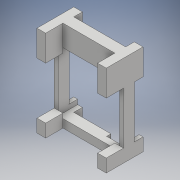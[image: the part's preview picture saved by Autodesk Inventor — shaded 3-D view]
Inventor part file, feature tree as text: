
AUTODESK INVENTOR PART (.ipt)
format: ipt  version: 2017 (Build 210142000, 142)  size: 410,624 bytes
history: native  units: mm
features: sketch x32, extrude x29
ambient origin geometry x8: Origin, YZ Plane, XZ Plane, XY Plane, X Axis, Y Axis, Z Axis, Center Point
bodies: Solid1 (feature_tree)
feature tree (61):
  extrude  "Extrusion1"  Depth=160.0mm
  extrude  "Extrusion2"  Depth=10.0mm
  extrude  "Extrusion3"  Depth=140.0mm
  extrude  "Extrusion4"  Depth=140.0mm TaperAngle=0.0deg
  extrude  "Extrusion5"  Depth=10.0mm
  extrude  "Extrusion6"  Depth=120.0mm
  extrude  "Extrusion7"  Depth=10.0mm
  extrude  "Extrusion8"  Depth=120.0mm
  extrude  "Extrusion9"  Depth=10.0mm
  extrude  "Extrusion10"  Depth=10.0mm
  extrude  "Extrusion11"  Depth=10.0mm TaperAngle=0.0deg
  extrude  "Extrusion12"  Depth=20.0mm
  sketch  "Sketch13"  dims[d29=10.0mm d30=0.0mm d31=10.0mm]
  extrude  "Extrusion13"  Depth=10.0mm
  extrude  "Extrusion14"  Depth=20.0mm
  extrude  "Extrusion15"  Depth=10.0mm
  extrude  "Extrusion16"  Depth=120.0mm
  sketch  "Sketch18"  dims[d42=1.0mm d43=0.0mm d44=1.0mm d45=0.0mm]
  extrude  "Extrusion17"  Depth=10.0mm TaperAngle=0.0deg
  sketch  "Sketch20"  dims[d50=10.0mm d51=0.0mm d52=10.0mm d53=0.0mm]
  extrude  "Extrusion18"  Depth=1.0mm TaperAngle=0.0deg
  extrude  "Extrusion19"  Depth=1.0mm TaperAngle=0.0deg
  extrude  "Extrusion20"  Depth=10.0mm TaperAngle=0.0deg
  extrude  "Extrusion21"  Depth=142.0mm
  extrude  "Extrusion22"  Depth=19.0mm TaperAngle=0.0deg
  extrude  "Extrusion23"  Depth=11.0mm TaperAngle=0.0deg
  extrude  "Extrusion24"  Depth=10.0mm
  extrude  "Extrusion25"  Depth=11.0mm TaperAngle=0.0deg
  extrude  "Extrusion26"  Depth=10.0mm
  extrude  "Extrusion27"  Depth=11.0mm TaperAngle=0.0deg
  extrude  "Extrusion28"  Depth=11.0mm TaperAngle=0.0deg
  extrude  "Extrusion29"  Depth=11.0mm
  sketch  "Sketch1"  dims[d0=160.0mm d1=190.0mm]
  sketch  "Sketch2"  dims[d2=55.0mm d3=0.0mm d4=10.0mm]
  sketch  "Sketch3"  dims[d5=10.0mm d6=140.0mm]
  sketch  "Sketch4"  dims[d7=140.0mm d8=35.0mm d9=0.0mm]
  sketch  "Sketch5"  dims[d10=10.0mm d11=10.0mm]
  sketch  "Sketch6"  dims[d12=120.0mm d13=120.0mm]
  sketch  "Sketch7"  dims[d14=20.0mm d15=0.0mm d16=10.0mm]
  sketch  "Sketch8"  dims[d17=10.0mm d18=120.0mm]
  sketch  "Sketch9"  dims[d19=120.0mm d20=10.0mm]
  sketch  "Sketch10"  dims[d21=120.0mm d22=10.0mm]
  sketch  "Sketch11"  dims[d23=20.0mm d24=0.0mm d25=10.0mm d26=0.0mm]
  sketch  "Sketch12"  dims[d27=120.0mm d28=20.0mm]
  sketch  "Sketch14"  dims[d32=10.0mm d33=20.0mm]
  sketch  "Sketch15"  dims[d34=10.0mm d35=10.0mm]
  sketch  "Sketch16"  dims[d36=45.0mm d37=0.0mm d38=120.0mm]
  sketch  "Sketch17"  dims[d39=20.0mm d40=10.0mm d41=0.0mm]
  sketch  "Sketch19"  dims[d46=1.0mm d47=0.0mm d48=1.0mm d49=0.0mm]
  sketch  "Sketch21"  dims[d54=45.0mm d55=0.0mm d56=142.0mm]
  sketch  "Sketch22"  dims[d57=10.0mm d58=19.0mm d59=0.0mm]
  sketch  "Sketch23"  dims[d60=11.0mm d61=0.0mm d62=11.0mm d63=0.0mm]
  sketch  "Sketch24"  dims[d64=142.0mm d65=10.0mm]
  sketch  "Sketch25"  dims[d66=9.0mm d67=0.0mm d68=11.0mm d69=0.0mm]
  sketch  "Sketch26"  dims[d70=142.0mm d71=10.0mm]
  sketch  "Sketch27"  dims[d72=9.0mm d73=0.0mm d74=11.0mm d75=0.0mm]
  sketch  "Sketch28"  dims[d76=11.0mm d77=0.0mm d78=50.0mm d79=0.0mm]
  sketch  "Sketch29"  dims[d80=11.0mm d81=11.0mm]
  sketch  "Sketch30"  dims[d82=120.0mm]
  sketch  "Sketch31"  dims[d83=10.0mm]
  sketch  "Sketch32"  dims[d84=50.0mm d85=0.0mm d86=34.0mm d87=20.0mm d88=10.0mm d89=19.0mm d90=0.0mm d91=19.0mm d92=0.0mm d93=20.0mm d94=0.0mm d95=10.0mm d96=0.0mm]
